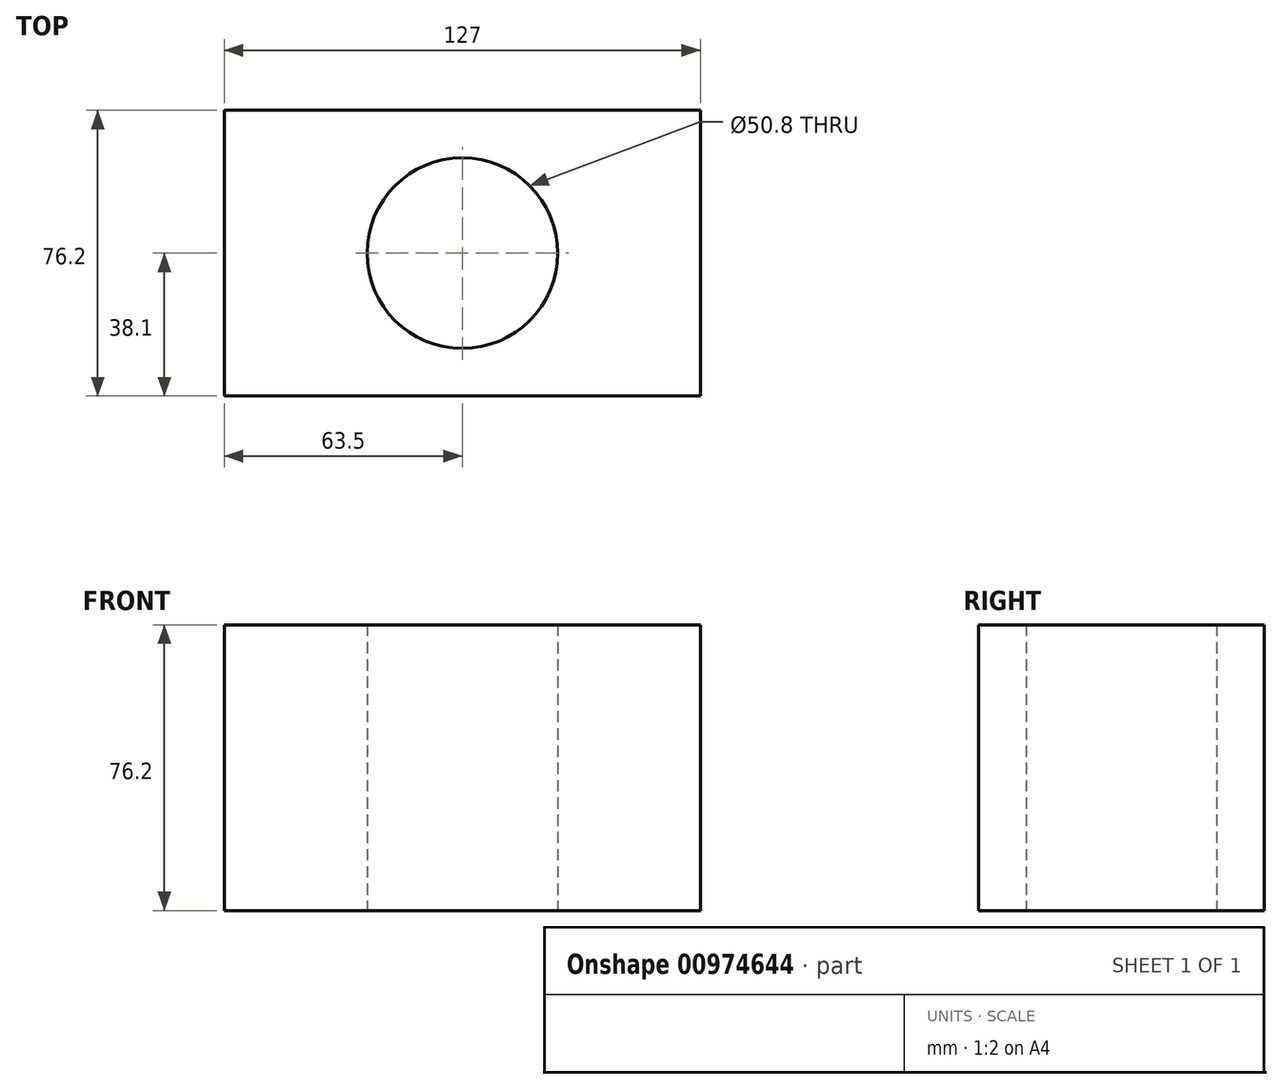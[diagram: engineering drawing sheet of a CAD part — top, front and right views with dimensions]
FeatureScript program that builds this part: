
annotation { "Feature Type Name" : "Feature", "Feature Type Description" : "" }
export const myFeature = defineFeature(function(context is Context, id is Id, definition is map)
    precondition{}
    {
        {
            var Q0;
            Q0=qCreatedBy(makeId("Top.planeOp"),FACE);
            var sketch = newSketch(context, id + "F0", { "sketchPlane" : qUnion([Q0])});
            skLineSegment(sketch, "E0.bottom", {"start": v(-63.5, 38.1) * mm, "end": v(63.5, 38.1) * mm});
            skLineSegment(sketch, "E0.top", {"start": v(-63.5, -38.1) * mm, "end": v(63.5, -38.1) * mm});
            skLineSegment(sketch, "E0.left", {"start": v(-63.5, 38.1) * mm, "end": v(-63.5, -38.1) * mm});
            skLineSegment(sketch, "E0.right", {"start": v(63.5, 38.1) * mm, "end": v(63.5, -38.1) * mm});
            skPoint(sketch, "E0.middle", {"position": v(0, 0) * mm});
            skCircle(sketch, "E1", {"center": v(0, 0) * mm, "radius": 25.4 * mm});
            skSolve(sketch);
        }
        {
            var Q0;
            Q0=makeQuery(id+"F0.imprint","IMPRINT",FACE,{"disambiguationData":[TD([[makeQuery(id+"F0.imprint","IMPRINT",EDGE,{"derivedFrom":sQuery(id+"F0.wireOp",EDGE,"E0.bottom")}),-1.0]])]});
            extrude(context, id + "F1", {"entities" : qUnion([Q0]), "depth" : 76.2 * mm, "offsetDistance" : 25.4 * mm});
        }
    });
